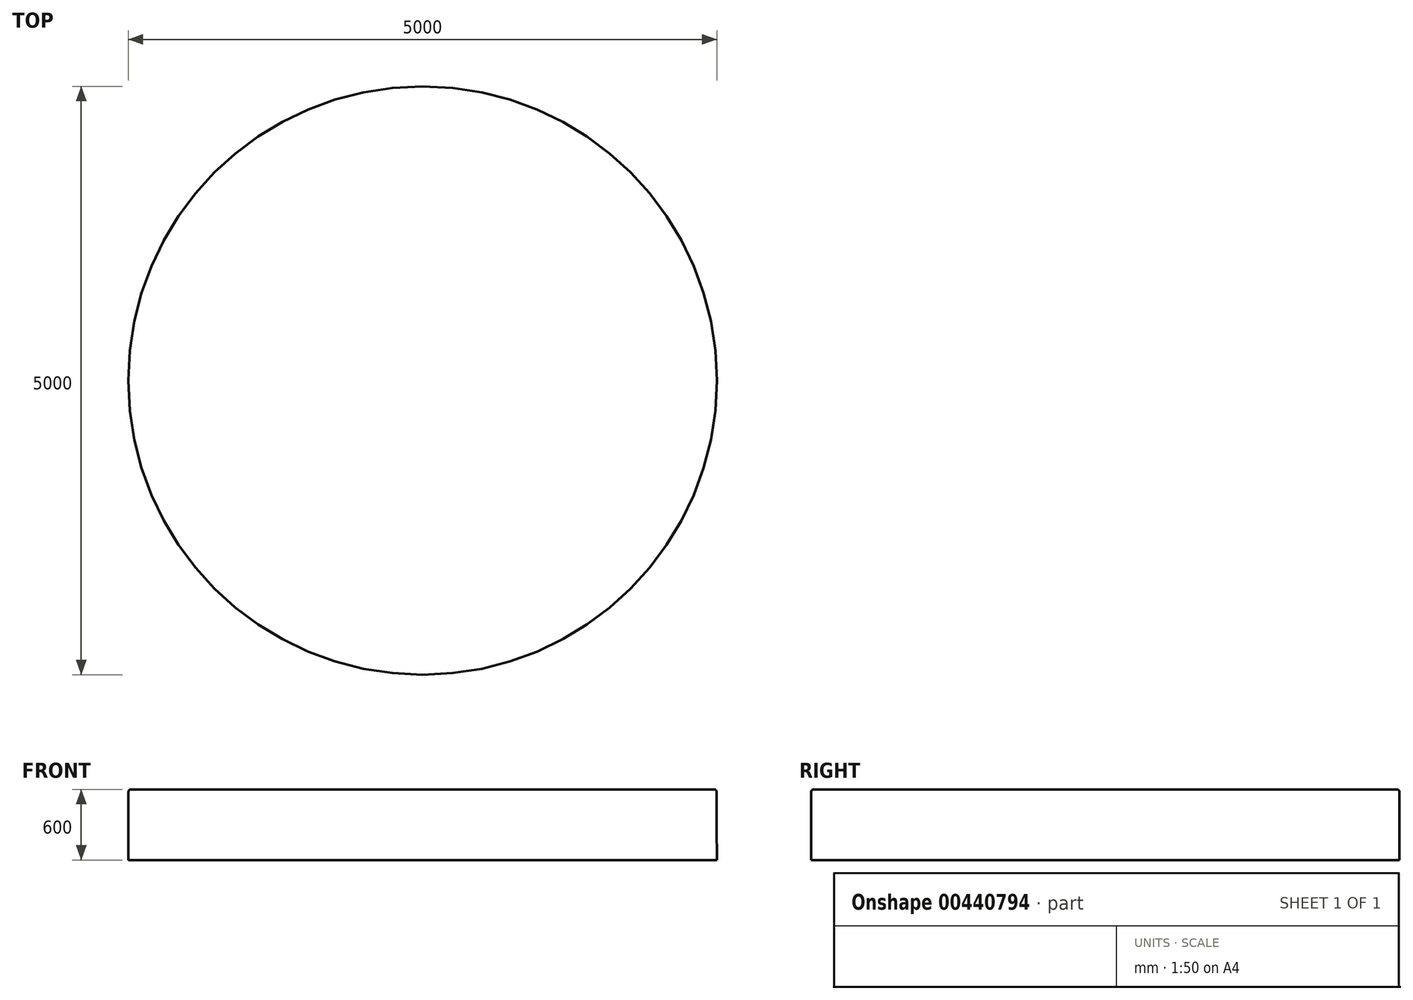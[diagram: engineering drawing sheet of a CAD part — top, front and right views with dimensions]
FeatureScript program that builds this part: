
annotation { "Feature Type Name" : "Feature", "Feature Type Description" : "" }
export const myFeature = defineFeature(function(context is Context, id is Id, definition is map)
    precondition{}
    {
        {
            var Q0;
            Q0=qCreatedBy(makeId("Top.planeOp"),FACE);
            var sketch = newSketch(context, id + "F0", { "sketchPlane" : qUnion([Q0])});
            skCircle(sketch, "E0", {"center": v(0, 0) * mm, "radius": 2500 * mm});
            skSolve(sketch);
        }
        {
            var Q0;
            Q0 = qSketchRegion(id + "F0", true);
            extrude(context, id + "F1", {"entities" : qUnion([Q0]), "depth" : 600 * mm, "hasDraft" : true, "draftAngle" : .2 * degree, "draftPullDirection" : true});
        }
        {
            var Q0;
            Q0=makeQuery(id+"F1.opExtrude","CAP_FACE",FACE,{"disambiguationData":[OSD([sQuery(id+"F0.wireOp",EDGE,"E0")])],"isStart":false});
            fillet(context, id + "F2", {"entities" : qUnion([Q0]), "radius" : 20 * mm, "tangentPropagation" : true, "allowEdgeOverflow" : false});
        }
    });
